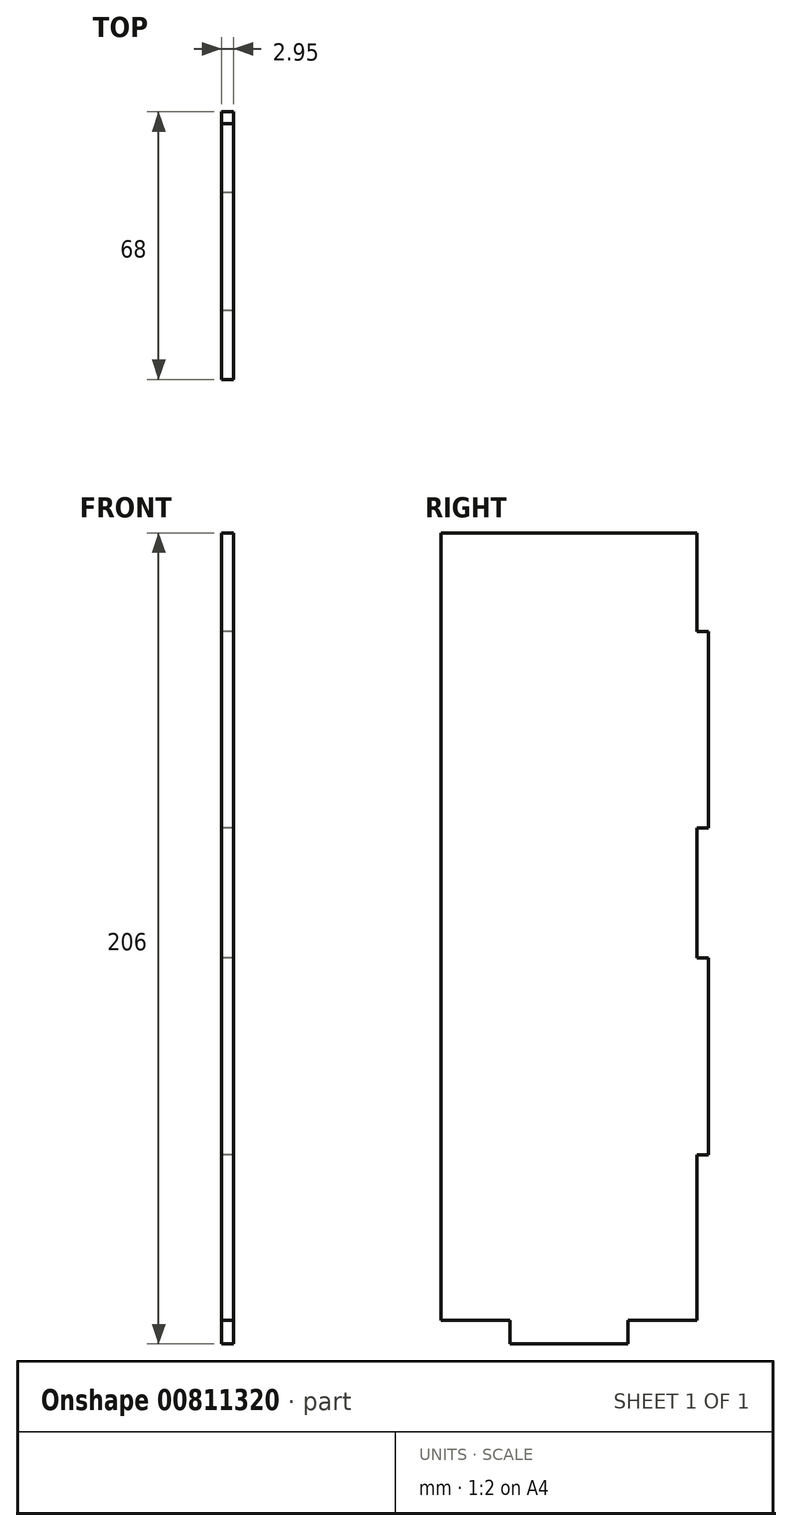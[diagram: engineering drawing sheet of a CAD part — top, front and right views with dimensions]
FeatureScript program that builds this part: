
annotation { "Feature Type Name" : "Feature", "Feature Type Description" : "" }
export const myFeature = defineFeature(function(context is Context, id is Id, definition is map)
    precondition{}
    {
        {
            var Q0;
            Q0=qCreatedBy(makeId("Right.planeOp"),FACE);
            var sketch = newSketch(context, id + "F0", { "sketchPlane" : qUnion([Q0])});
            skLineSegment(sketch, "E0.bottom", {"start": v(0, 8.05) * mm, "end": v(17.5, 8.05) * mm});
            skLineSegment(sketch, "E0.top", {"start": v(0, 208.05) * mm, "end": v(65, 208.05) * mm});
            skLineSegment(sketch, "E0.left", {"start": v(0, 8.05) * mm, "end": v(0, 208.05) * mm});
            skLineSegment(sketch, "E0.right", {"start": v(65, 8.05) * mm, "end": v(65, 50.05) * mm});
            skLineSegment(sketch, "E1.top", {"start": v(17.5, 2.05) * mm, "end": v(47.5, 2.05) * mm});
            skLineSegment(sketch, "E1.left", {"start": v(17.5, 8.05) * mm, "end": v(17.5, 2.05) * mm});
            skLineSegment(sketch, "E1.right", {"start": v(47.5, 8.05) * mm, "end": v(47.5, 2.05) * mm});
            skLineSegment(sketch, "E2", {"start": v(65, 8.05) * mm, "end": v(47.5, 8.05) * mm});
            skLineSegment(sketch, "E3.bottom", {"start": v(65, 183.05) * mm, "end": v(68, 183.05) * mm});
            skLineSegment(sketch, "E3.top", {"start": v(65, 133.05) * mm, "end": v(68, 133.05) * mm});
            skLineSegment(sketch, "E3.right", {"start": v(68, 183.05) * mm, "end": v(68, 133.05) * mm});
            skLineSegment(sketch, "E4.bottom", {"start": v(65, 100.05) * mm, "end": v(68, 100.05) * mm});
            skLineSegment(sketch, "E4.top", {"start": v(65, 50.05) * mm, "end": v(68, 50.05) * mm});
            skLineSegment(sketch, "E4.right", {"start": v(68, 100.05) * mm, "end": v(68, 50.05) * mm});
            skLineSegment(sketch, "E5.trimOffspring", {"start": v(65, 100.05) * mm, "end": v(65, 133.05) * mm});
            skLineSegment(sketch, "E6", {"start": v(65, 208.05) * mm, "end": v(65, 183.05) * mm});
            skSolve(sketch);
        }
        {
            var Q0;
            Q0=makeQuery(id+"F0.imprint","IMPRINT",FACE,{"disambiguationData":[TD([[makeQuery(id+"F0.imprint","IMPRINT",EDGE,{"derivedFrom":sQuery(id+"F0.wireOp",EDGE,"E0.bottom")}),1.0]])]});
            extrude(context, id + "F1", {"entities" : qUnion([Q0]), "depth" : 2.95 * mm, "offsetDistance" : 25 * mm});
        }
    });
